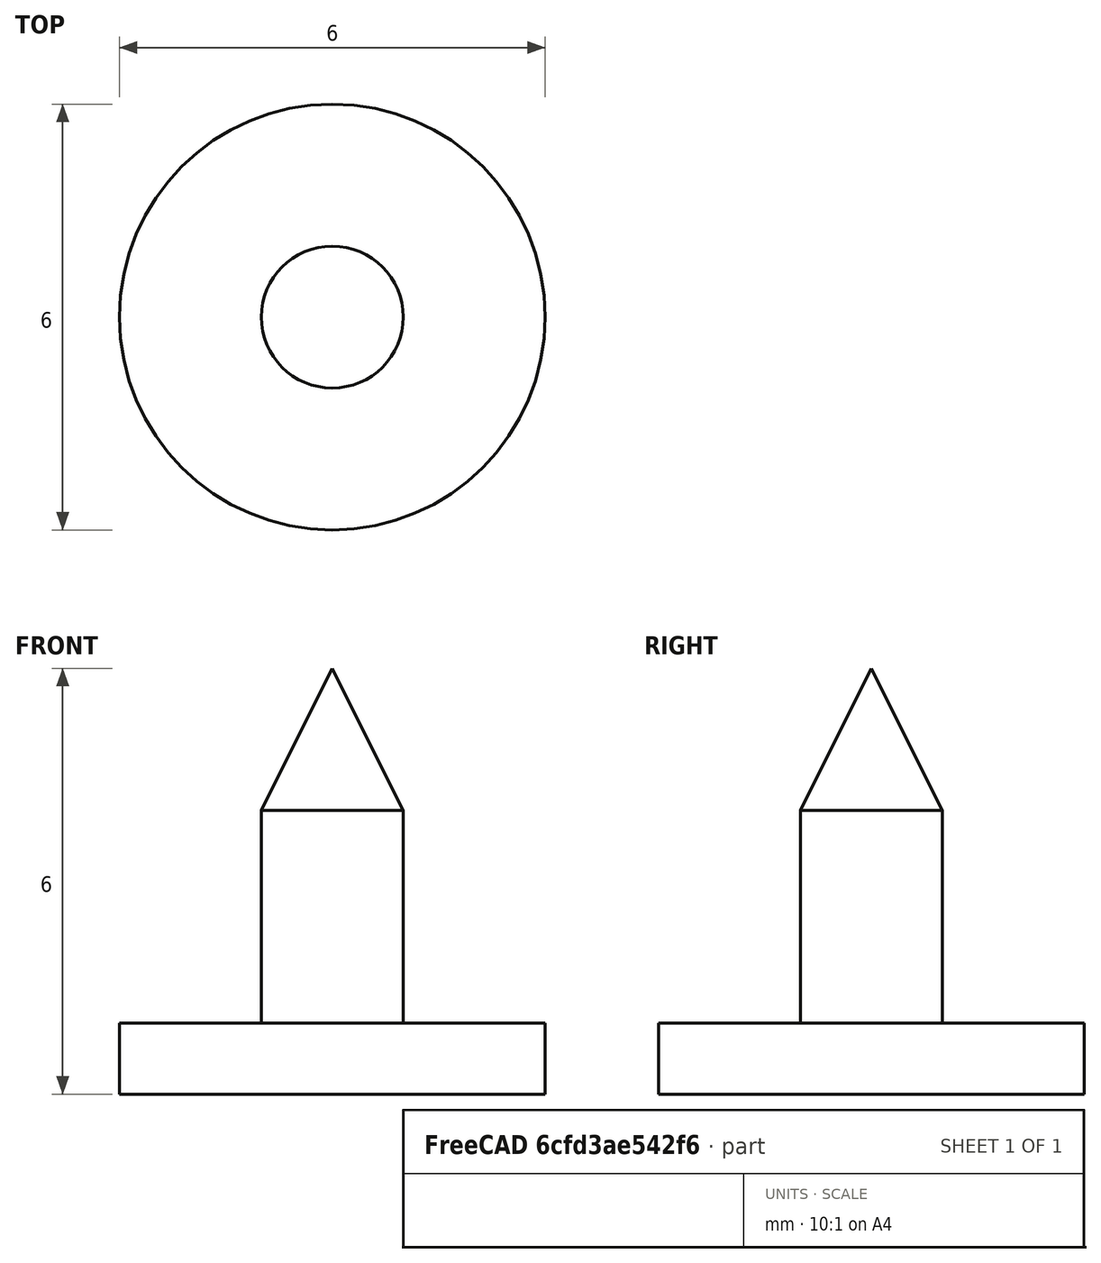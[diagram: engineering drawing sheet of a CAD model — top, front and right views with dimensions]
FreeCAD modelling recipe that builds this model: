
FCSTD DOCUMENT  (FreeCAD 0.20R29603 (Git))
Label: sprinkler plug
License: All rights reserved
LicenseURL: http://en.wikipedia.org/wiki/All_rights_reserved
objects: PartDesign::AdditiveCylinder×2, PartDesign::AdditiveCone×1, PartDesign::Body×1
note: 7 computed .brp shape members not serialized (recipe doc carries the construction recipe); baked Part::Feature solids carry a one-line shape summary decoded from their .brp

FEATURE [PartDesign::AdditiveCylinder] Cylinder
  Angle = 360
  AttacherType = Attacher::AttachEngine3D
  FirstAngle = 0
  Height = 1
  MapMode = 5
  Radius = 3
  SecondAngle = 0
  Support = -> [XY_Plane]
FEATURE [PartDesign::AdditiveCylinder] Cylinder001
  Angle = 360
  AttacherType = Attacher::AttachEngine3D
  BaseFeature = -> Cylinder
  FirstAngle = 0
  Height = 4
  MapMode = 2
  Radius = 1
  SecondAngle = 0
  Support = -> [Cylinder]
FEATURE [PartDesign::AdditiveCone] Cone
  Angle = 360
  AttacherType = Attacher::AttachEngine3D
  BaseFeature = -> Cylinder001
  Height = 2
  MapMode = 5
  Placement = pos=(0,0,4) rot=(0,0,1;0rad)
  Radius1 = 1
  Radius2 = 0
  Support = -> [Cylinder001]
FEATURE [PartDesign::Body] Body
  Group = -> [Cylinder,Cylinder001,Cone]
  Origin = -> Origin
  Tip = -> Cone
